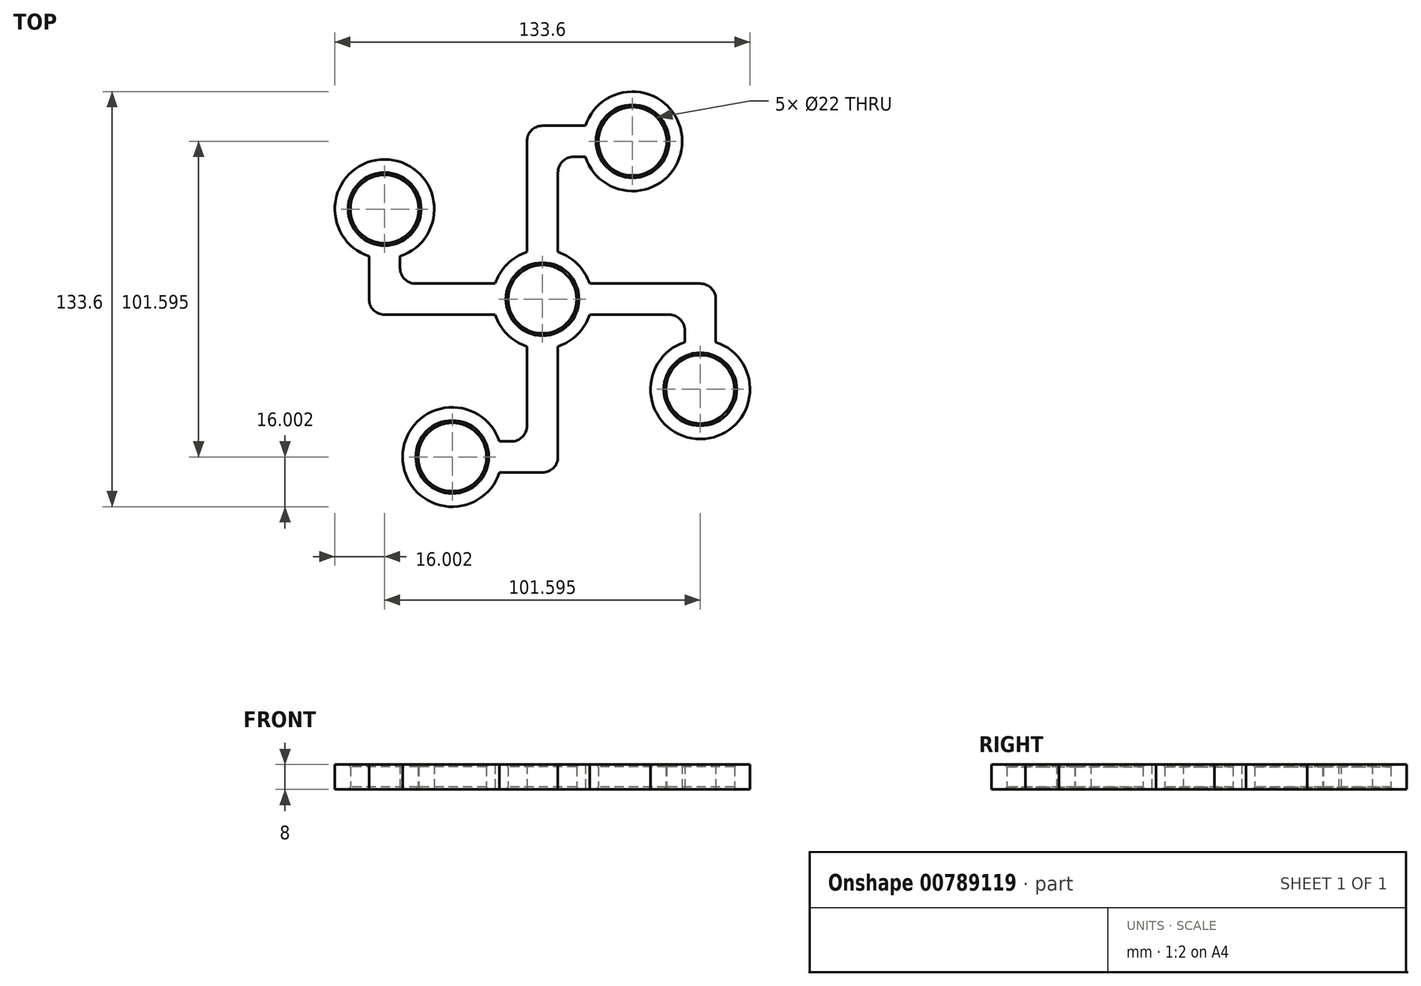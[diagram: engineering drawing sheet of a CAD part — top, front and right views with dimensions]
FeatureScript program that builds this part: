
annotation { "Feature Type Name" : "Feature", "Feature Type Description" : "" }
export const myFeature = defineFeature(function(context is Context, id is Id, definition is map)
    precondition{}
    {
        {
            var Q0;
            Q0=qCreatedBy(makeId("Top.planeOp"),FACE);
            var sketch = newSketch(context, id + "F0", { "sketchPlane" : qUnion([Q0])});
            skCircle(sketch, "E0", {"center": v(0, 0) * mm, "radius": 11 * mm});
            skCircle(sketch, "E1", {"center": v(0, 0) * mm, "radius": 16 * mm});
            skLineSegment(sketch, "E2", {"start": v(0, 0) * mm, "end": v(0, 50.8) * mm});
            skLineSegment(sketch, "E3", {"start": v(0, 50.8) * mm, "end": v(13, 50.8) * mm});
            skCircle(sketch, "E4", {"center": v(29, 50.8) * mm, "radius": 11 * mm});
            skCircle(sketch, "E5", {"center": v(29, 50.8) * mm, "radius": 16 * mm});
            skLineSegment(sketch, "E6.0", {"start": v(5, 15.2) * mm, "end": v(5, 40.8) * mm});
            skLineSegment(sketch, "E7.0", {"start": v(-5, 15.2) * mm, "end": v(-5, 50.8) * mm});
            skLineSegment(sketch, "E8.0", {"start": v(10, 45.8) * mm, "end": v(13.8, 45.8) * mm});
            skLineSegment(sketch, "E9.0", {"start": v(0, 55.8) * mm, "end": v(13.8, 55.8) * mm});
            skArc(sketch, "E10.filletArc", {"start": v(0, 55.8) * mm, "mid": v(-3.54, 54.33) * mm, "end": v(-5, 50.8) * mm});
            skArc(sketch, "E11.filletArc", {"start": v(10, 45.8) * mm, "mid": v(6.46, 44.33) * mm, "end": v(5, 40.8) * mm});
            skLineSegment(sketch, "E12", {"start": v(-5, 0) * mm, "end": v(5, 0) * mm});
            skSolve(sketch);
        }
        {
            var Q0;
            Q0=makeQuery(id+"F0.imprint","IMPRINT",FACE,{"disambiguationData":[TD([[makeQuery(id+"F0.imprint","IMPRINT",EDGE,{"derivedFrom":sQuery(id+"F0.wireOp",EDGE,"E4")}),-1.0]])]});
            var Q1;
            {var subQ1=sQuery(id+"F0.wireOp",EDGE,"E3");Q1=makeQuery(id+"F0.imprint","IMPRINT",FACE,{"disambiguationData":[TD([[makeQuery(id+"F0.imprint","IMPRINT",EDGE,{"derivedFrom":subQ1}),-1.0]])]});}
            var Q2;
            {var subQ0=sQuery(id+"F0.wireOp",EDGE,"E3");Q2=makeQuery(id+"F0.imprint","IMPRINT",FACE,{"disambiguationData":[TD([[makeQuery(id+"F0.imprint","IMPRINT",EDGE,{"derivedFrom":subQ0}),1.0]])]});}
            var Q3;
            Q3=makeQuery(id+"F0.imprint","IMPRINT",FACE,{"disambiguationData":[TD([[makeQuery(id+"F0.imprint","IMPRINT",EDGE,{"derivedFrom":sQuery(id+"F0.wireOp",EDGE,"E0")}),-1.0]])]});
            var Q4;
            Q4 = qSketchRegion(id + "F2", true);
            extrude(context, id + "F1", {"entities" : qUnion([Q0, Q1, Q2, Q3, Q4]), "depth" : 8 * mm, "offsetDistance" : 25 * mm});
        }
        {
            var Q0;
            Q0=qCreatedBy(makeId("Front.planeOp"),FACE);
            var sketch = newSketch(context, id + "F2", { "sketchPlane" : qUnion([Q0])});
            skLineSegment(sketch, "E13", {"start": v(0, 0) * mm, "end": v(0, 47.95) * mm});
            skSolve(sketch);
        }
        {
            var Q0;
            Q0=makeQuery(id+"F1.opExtrude","SWEPT_BODY",BODY,{"disambiguationData":[OSD([sQuery(id+"F0.wireOp",EDGE,"E0"),sQuery(id+"F0.wireOp",EDGE,"E1"),sQuery(id+"F0.wireOp",EDGE,"E4"),sQuery(id+"F0.wireOp",EDGE,"E5"),sQuery(id+"F0.wireOp",EDGE,"E6.0"),sQuery(id+"F0.wireOp",EDGE,"E7.0"),sQuery(id+"F0.wireOp",EDGE,"E8.0"),sQuery(id+"F0.wireOp",EDGE,"E9.0"),sQuery(id+"F0.wireOp",EDGE,"E10.filletArc"),sQuery(id+"F0.wireOp",EDGE,"E11.filletArc")])]});
            var Q1;
            Q1=sQuery(id+"F2.wireOp",EDGE,"E13");
            circularPattern(context, id + "F3", {"operationType" : NewBodyOperationType.ADD, "entities" : qUnion([Q0]), "axis" : qUnion([Q1]), "angle" : 360 * degree, "instanceCount" : 4, "equalSpace" : true});
        }
        {
            var Q0;
            Q0=makeQuery(id+"F3.opPattern","COPY",EDGE,{"derivedFrom":makeQuery(id+"F1.opExtrude","CAP_EDGE",EDGE,{"disambiguationData":[OSD([sQuery(id+"F0.wireOp",EDGE,"E4")])],"isStart":false}),"instanceName":"2"});
            var Q1;
            Q1=makeQuery(id+"F3.opPattern","COPY",EDGE,{"derivedFrom":makeQuery(id+"F1.opExtrude","CAP_EDGE",EDGE,{"disambiguationData":[OSD([sQuery(id+"F0.wireOp",EDGE,"E4")])],"isStart":false}),"instanceName":"1"});
            var Q2;
            Q2=makeQuery(id+"F1.opExtrude","CAP_EDGE",EDGE,{"disambiguationData":[OSD([sQuery(id+"F0.wireOp",EDGE,"E4")])],"isStart":false});
            var Q3;
            Q3=makeQuery(id+"F3.opPattern","COPY",EDGE,{"derivedFrom":makeQuery(id+"F1.opExtrude","CAP_EDGE",EDGE,{"disambiguationData":[OSD([sQuery(id+"F0.wireOp",EDGE,"E4")])],"isStart":false}),"instanceName":"5"});
            var Q4;
            Q4=makeQuery(id+"F3.opPattern","COPY",EDGE,{"derivedFrom":makeQuery(id+"F1.opExtrude","CAP_EDGE",EDGE,{"disambiguationData":[OSD([sQuery(id+"F0.wireOp",EDGE,"E4")])],"isStart":false}),"instanceName":"3"});
            var Q5;
            Q5=makeQuery(id+"F3.opPattern","COPY",EDGE,{"derivedFrom":makeQuery(id+"F1.opExtrude","CAP_EDGE",EDGE,{"disambiguationData":[OSD([sQuery(id+"F0.wireOp",EDGE,"E4")])],"isStart":false}),"instanceName":"4"});
            var Q6;
            Q6=makeQuery(id+"F1.opExtrude","CAP_EDGE",EDGE,{"disambiguationData":[OSD([sQuery(id+"F0.wireOp",EDGE,"E0")])],"isStart":false});
            var Q7;
            Q7=makeQuery(id+"F3.opPattern","COPY",EDGE,{"derivedFrom":makeQuery(id+"F1.opExtrude","CAP_EDGE",EDGE,{"disambiguationData":[OSD([sQuery(id+"F0.wireOp",EDGE,"E4")])],"isStart":true}),"instanceName":"3"});
            var Q8;
            Q8=makeQuery(id+"F3.opPattern","COPY",EDGE,{"derivedFrom":makeQuery(id+"F1.opExtrude","CAP_EDGE",EDGE,{"disambiguationData":[OSD([sQuery(id+"F0.wireOp",EDGE,"E4")])],"isStart":true}),"instanceName":"4"});
            var Q9;
            Q9=makeQuery(id+"F3.opPattern","COPY",EDGE,{"derivedFrom":makeQuery(id+"F1.opExtrude","CAP_EDGE",EDGE,{"disambiguationData":[OSD([sQuery(id+"F0.wireOp",EDGE,"E4")])],"isStart":true}),"instanceName":"5"});
            var Q10;
            Q10=makeQuery(id+"F1.opExtrude","CAP_EDGE",EDGE,{"disambiguationData":[OSD([sQuery(id+"F0.wireOp",EDGE,"E4")])],"isStart":true});
            var Q11;
            Q11=makeQuery(id+"F3.opPattern","COPY",EDGE,{"derivedFrom":makeQuery(id+"F1.opExtrude","CAP_EDGE",EDGE,{"disambiguationData":[OSD([sQuery(id+"F0.wireOp",EDGE,"E4")])],"isStart":true}),"instanceName":"1"});
            var Q12;
            Q12=makeQuery(id+"F1.opExtrude","CAP_EDGE",EDGE,{"disambiguationData":[OSD([sQuery(id+"F0.wireOp",EDGE,"E0")])],"isStart":true});
            var Q13;
            Q13=makeQuery(id+"F3.opPattern","COPY",EDGE,{"derivedFrom":makeQuery(id+"F1.opExtrude","CAP_EDGE",EDGE,{"disambiguationData":[OSD([sQuery(id+"F0.wireOp",EDGE,"E4")])],"isStart":true}),"instanceName":"2"});
            chamfer(context, id + "F4", {"entities" : qUnion([Q0, Q1, Q2, Q3, Q4, Q5, Q6, Q7, Q8, Q9, Q10, Q11, Q12, Q13]), "width" : 0.76 * mm, "tangentPropagation" : true});
        }
    });
